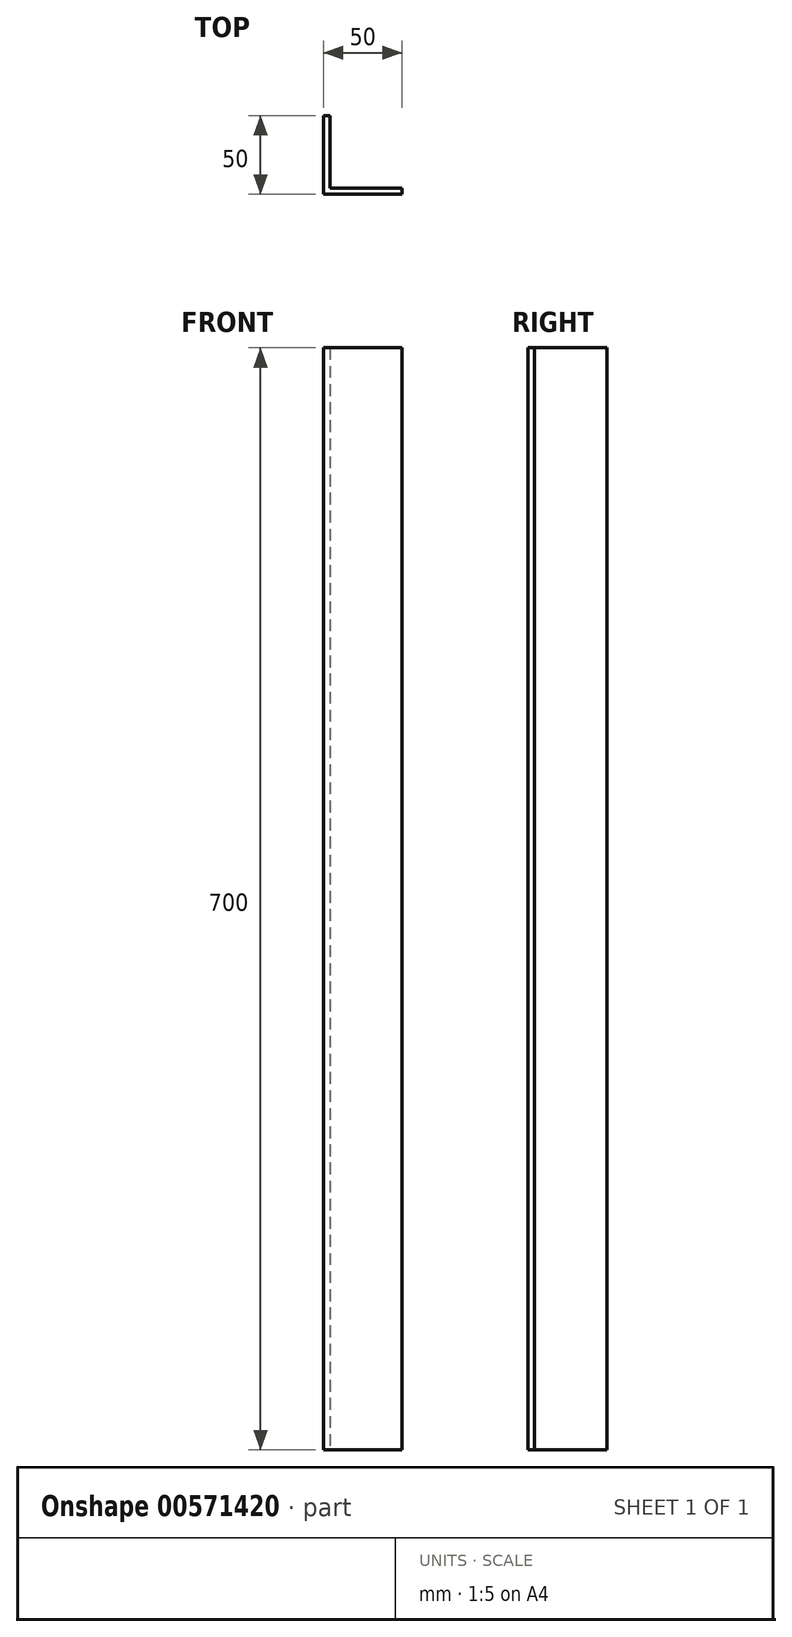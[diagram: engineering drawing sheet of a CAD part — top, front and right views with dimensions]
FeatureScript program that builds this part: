
annotation { "Feature Type Name" : "Feature", "Feature Type Description" : "" }
export const myFeature = defineFeature(function(context is Context, id is Id, definition is map)
    precondition{}
    {
        {
            var Q0;
            Q0=qCreatedBy(makeId("Top.planeOp"),FACE);
            var sketch = newSketch(context, id + "F0", { "sketchPlane" : qUnion([Q0])});
            skLineSegment(sketch, "E0", {"start": v(0, 0) * mm, "end": v(0, 50) * mm});
            skLineSegment(sketch, "E1", {"start": v(0, 50) * mm, "end": v(4, 50) * mm});
            skLineSegment(sketch, "E2", {"start": v(4, 50) * mm, "end": v(4, 4) * mm});
            skLineSegment(sketch, "E3", {"start": v(4, 4) * mm, "end": v(50, 4) * mm});
            skLineSegment(sketch, "E4", {"start": v(50, 4) * mm, "end": v(50, 0) * mm});
            skLineSegment(sketch, "E5", {"start": v(50, 0) * mm, "end": v(0, 0) * mm});
            skSolve(sketch);
        }
        {
            var Q0;
            Q0=makeQuery(id+"F0.imprint","IMPRINT",FACE,{"disambiguationData":[TD([[makeQuery(id+"F0.imprint","IMPRINT",EDGE,{"derivedFrom":sQuery(id+"F0.wireOp",EDGE,"E0")}),-1.0]])]});
            extrude(context, id + "F1", {"entities" : qUnion([Q0]), "depth" : 700 * mm, "offsetDistance" : 25 * mm});
        }
    });
